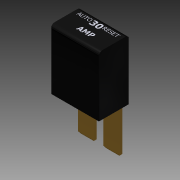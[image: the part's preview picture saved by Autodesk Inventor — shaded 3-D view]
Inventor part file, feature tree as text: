
AUTODESK INVENTOR PART (.ipt)
format: ipt  version: 2014 (Build 180170000, 170)  size: 481,280 bytes
history: native  units: in
note: dims shown in document units (in); Inventor stores cm internally (conversion verified against a paired STEP export)
features: sketch x6, extrude x4, plane x3, emboss x2, fillet x1, mirror x1
ambient origin geometry x8: Origin, YZ Plane, XZ Plane, XY Plane, X Axis, Y Axis, Z Axis, Center Point
bodies: Solid1 (feature_tree)
feature tree (17):
  extrude  "Extrusion1"  Depth=0.39in
  fillet  "Fillet1"  Radius=0.78in
  extrude  "Extrusion3"  Depth=0.212in
  extrude  "Extrusion4"  Depth=0.0585in
  extrude  "Extrusion5"  Depth=0.57in TaperAngle=0.0deg
  plane  "Work Plane1"
  mirror  "Mirror1"
  plane  "Work Plane2"
  emboss  "Emboss1"
  plane  "Work Plane4"
  emboss  "Emboss3"
  sketch  "Sketch1"  dims[d0=0.62in d1=0.39in d2=0.78in d3=0.0in]
  sketch  "Sketch2"  dims[d4=0.01in d5=0.05in d6=0.212in]
  sketch  "Sketch3"  dims[d8=0.031in d13=0.0585in]
  sketch  "Sketch4"  dims[d14=0.57in d15=0.0in d16=0.57in d17=0.0in]
  sketch  "Sketch6"  dims[d18=0.023in]
  sketch  "Sketch8"  dims[d19=0.023in d20=0.023in d21=0.57in d22=0.0in d26=0.1875in d27=0.0001in d28=0.0in d32=0.1875in d33=0.0001in d34=0.0in]
